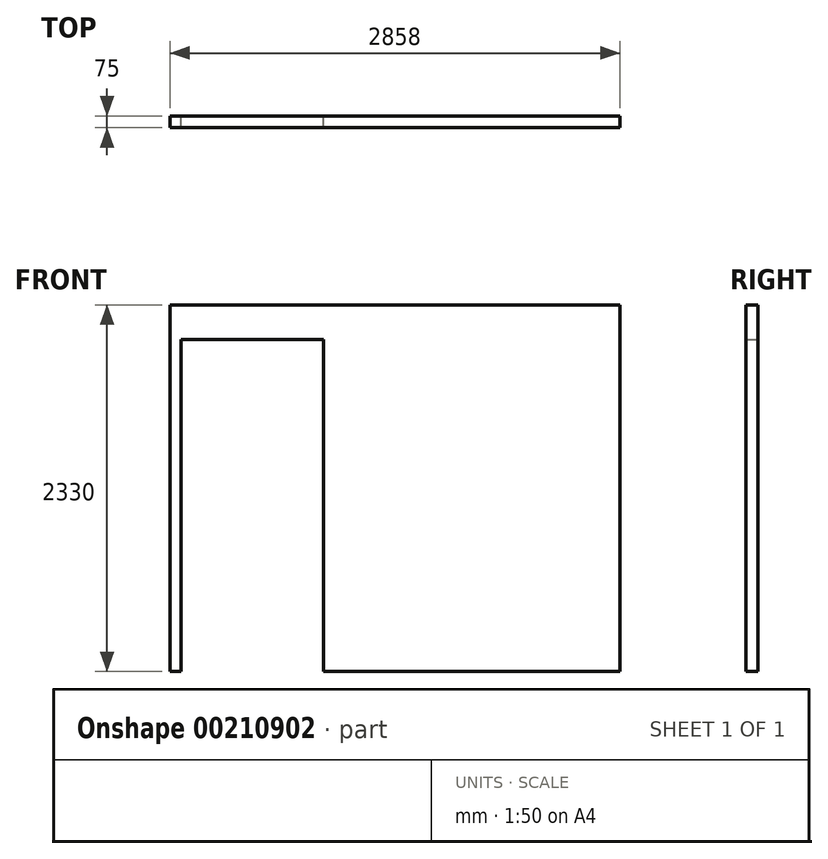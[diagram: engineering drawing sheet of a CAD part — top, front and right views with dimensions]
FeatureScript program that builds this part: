
annotation { "Feature Type Name" : "Feature", "Feature Type Description" : "" }
export const myFeature = defineFeature(function(context is Context, id is Id, definition is map)
    precondition{}
    {
        {
            var Q0;
            Q0=qCreatedBy(makeId("Front.planeOp"),FACE);
            var sketch = newSketch(context, id + "F0", { "sketchPlane" : qUnion([Q0])});
            skLineSegment(sketch, "E0.bottom", {"start": v(0, 0) * mm, "end": v(2858, 0) * mm});
            skLineSegment(sketch, "E0.top", {"start": v(0, 2330) * mm, "end": v(2858, 2330) * mm});
            skLineSegment(sketch, "E0.left", {"start": v(0, 0) * mm, "end": v(0, 2330) * mm});
            skLineSegment(sketch, "E0.right", {"start": v(2858, 0) * mm, "end": v(2858, 2330) * mm});
            skLineSegment(sketch, "E1.bottom", {"start": v(70, 0) * mm, "end": v(975, 0) * mm});
            skLineSegment(sketch, "E1.top", {"start": v(70, 2110) * mm, "end": v(975, 2110) * mm});
            skLineSegment(sketch, "E1.left", {"start": v(70, 0) * mm, "end": v(70, 2110) * mm});
            skLineSegment(sketch, "E1.right", {"start": v(975, 0) * mm, "end": v(975, 2110) * mm});
            skSolve(sketch);
        }
        {
            var Q0;
            Q0=makeQuery(id+"F0.imprint","IMPRINT",FACE,{"disambiguationData":[TD([[makeQuery(id+"F0.imprint","IMPRINT",EDGE,{"derivedFrom":sQuery(id+"F0.wireOp",EDGE,"E0.bottom")}),1.0]])]});
            extrude(context, id + "F1", {"entities" : qUnion([Q0]), "depth" : 75 * mm});
        }
    });
